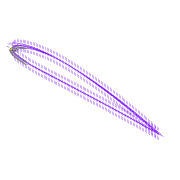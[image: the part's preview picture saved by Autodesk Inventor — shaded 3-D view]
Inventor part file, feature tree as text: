
AUTODESK INVENTOR PART (.ipt)
format: ipt  version: 2022 (Build 260153000, 153)  size: 523,776 bytes
history: native  units: mm
features: extrude x7, sketch x7, projected_geometry x6, fillet x3, shell x1, plane x1, pattern_linear x1
ambient origin geometry x8: Origin, YZ Plane, XZ Plane, XY Plane, X Axis, Y Axis, Z Axis, Center Point
bodies: Solid1 (feature_tree)
feature tree (26):
  extrude  "Extrusion1"  Depth=3.0mm
  shell  "Shell1"  Thickness=6.454mm
  plane  "Work Plane3"
  extrude  "Extrusion10"  Depth=12.0mm
  fillet  "Fillet2"  Radius=18.0mm
  fillet  "Fillet3"  Radius=13.0mm
  fillet  "Fillet4"  Radius=13.0mm
  extrude  "Extrusion11"  Depth=1.5mm
  extrude  "Extrusion12"  Depth=8.0mm TaperAngle=0.0deg
  pattern_linear  "Rectangular Pattern1"  Spacing1=4.0mm  [1 undecoded]
  extrude  "Extrusion14"  Depth=20.0mm TaperAngle=0.0deg
  extrude  "Extrusion15"  Depth=100.0mm TaperAngle=0.0deg
  extrude  "Extrusion13"  [1 undecoded]
  sketch  "Sketch3"  dims[d0=60.0mm d1=0.0mm d2=3.0mm d74=6.454mm]
  sketch  "Sketch29"  dims[d75=63.621mm d76=12.0mm d77=18.0mm d78=13.0mm d79=13.0mm]
  projected_geometry  "Projected Loop14"
  sketch  "Sketch31"  dims[d80=5.0mm d81=1.5mm]
  sketch  "Sketch32"  dims[d82=1.5mm d83=8.0mm d84=0.0mm]
  projected_geometry  "Projected Loop15"
  sketch  "Sketch34"  dims[d85=1.0mm]
  projected_geometry  "Projected Loop16"
  sketch  "Sketch35"  dims[d86=2.7mm]
  sketch  "Sketch36"  dims[d87=4.0mm d88=4.0mm d89=20.0mm d90=0.0mm d91=100.0mm d92=0.0mm d93=-8.0mm d94=20.0mm d96=30.0mm d97=2.0mm d98=10.0mm d99=10.0mm d100=10.0mm d101=0.6mm d102=2.0mm d103=1.0mm d104=1.0mm d105=1.0mm d106=2.0mm d107=1.0mm d108=2.0mm d109=1.0mm d110=2.0mm d111=1.0mm d112=2.0mm d113=2.0mm d114=1.0mm d115=2.0mm d116=3.0mm d117=1.0mm d118=2.0mm d119=3.0mm d120=1.0mm d121=2.0mm d122=4.0mm d123=1.0mm d124=2.0mm d125=4.0mm d126=1.0mm d127=2.0mm d128=1.0mm d129=2.0mm d130=2.0mm d131=1.0mm d132=5.0mm d133=5.0mm d134=5.0mm d135=1.0mm d136=2.0mm d137=1.0mm d138=2.0mm d139=2.0mm d140=1.0mm d141=5.0mm d142=5.0mm d143=5.0mm d144=2.0mm d145=1.0mm d146=5.0mm d147=2.0mm d148=1.0mm d149=5.0mm d150=120.0mm d151=0.0mm d152=52.0mm d153=0.0mm d154=3.0mm d155=30.0deg d156=10.0mm d157=100.0mm d158=0.0mm]
  projected_geometry  "Projected Loop17"
  projected_geometry  "Projected Loop18"
  projected_geometry  "Projected Loop19"
note: 2 required parameter values undecoded (feature->parameter linkage not recoverable at this tier; creation-order binding heuristic only, values carry confidence <= 0.55)
